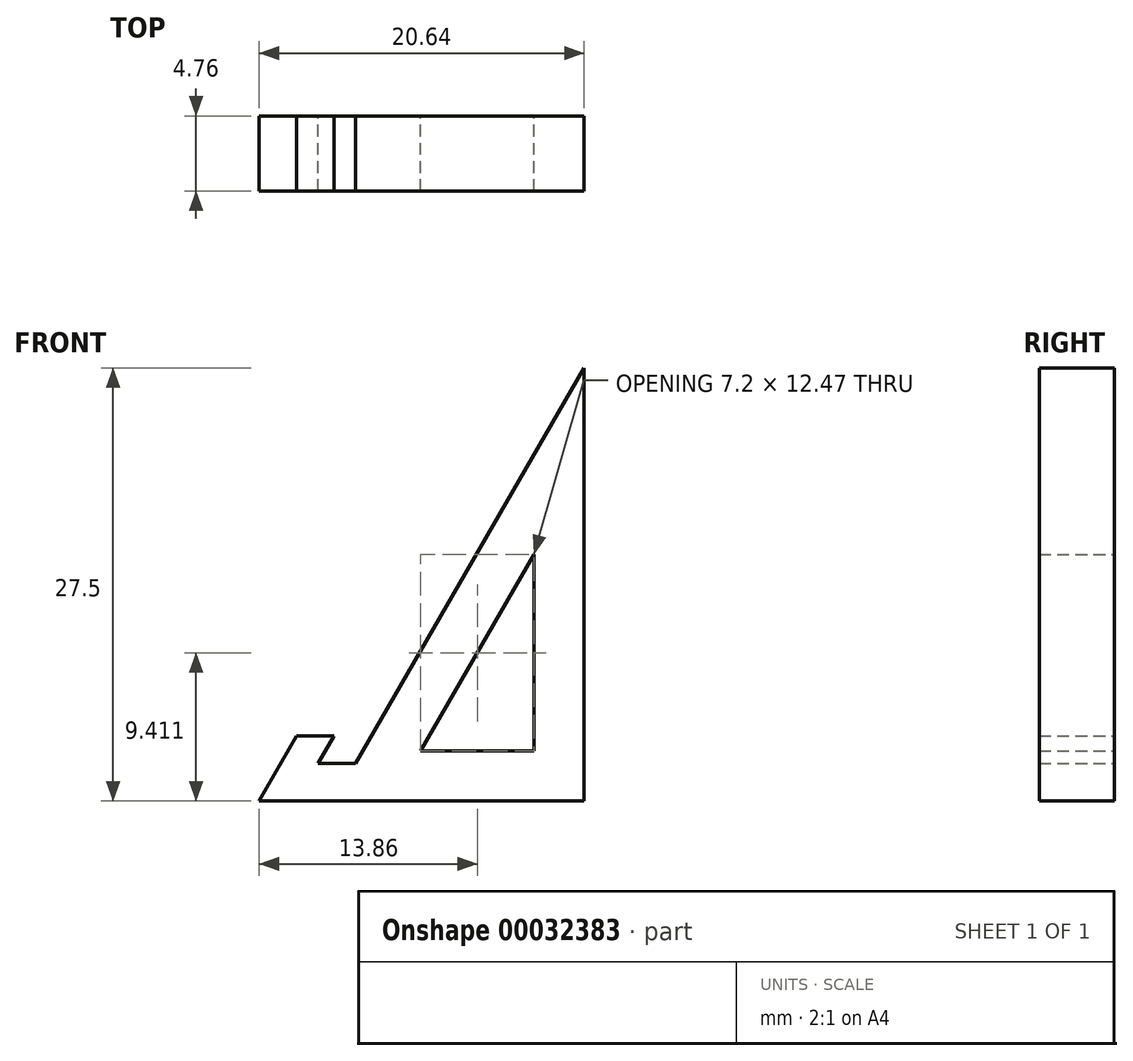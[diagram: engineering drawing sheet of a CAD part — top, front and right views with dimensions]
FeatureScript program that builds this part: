
annotation { "Feature Type Name" : "Feature", "Feature Type Description" : "" }
export const myFeature = defineFeature(function(context is Context, id is Id, definition is map)
    precondition{}
    {
        {
            var Q0;
            Q0=qCreatedBy(makeId("Front.planeOp"),FACE);
            var sketch = newSketch(context, id + "F0", { "sketchPlane" : qUnion([Q0])});
            skLineSegment(sketch, "E0", {"start": v(0, 0) * mm, "end": v(15.87, 0) * mm});
            skLineSegment(sketch, "E1", {"start": v(15.87, 0) * mm, "end": v(15.87, 27.5) * mm});
            skLineSegment(sketch, "E2", {"start": v(15.87, 27.5) * mm, "end": v(1.37, 2.38) * mm});
            skLineSegment(sketch, "E3.0", {"start": v(5.5, 3.18) * mm, "end": v(12.7, 3.18) * mm});
            skLineSegment(sketch, "E3.1", {"start": v(12.7, 15.65) * mm, "end": v(5.5, 3.17) * mm});
            skLineSegment(sketch, "E3.2", {"start": v(12.7, 3.18) * mm, "end": v(12.7, 15.65) * mm});
            skLineSegment(sketch, "E4", {"start": v(0, 0) * mm, "end": v(-4.76, 0) * mm});
            skLineSegment(sketch, "E5", {"start": v(-4.76, 0) * mm, "end": v(-2.38, 4.12) * mm});
            skLineSegment(sketch, "E6", {"start": v(-2.38, 4.12) * mm, "end": v(0, 4.12) * mm});
            skLineSegment(sketch, "E7", {"start": v(0, 4.12) * mm, "end": v(-1, 2.38) * mm});
            skLineSegment(sketch, "E8", {"start": v(-1, 2.38) * mm, "end": v(1.37, 2.38) * mm});
            skSolve(sketch);
        }
        {
            var Q0;
            Q0 = qSketchRegion(id + "F0", true);
            extrude(context, id + "F1", {"entities" : qUnion([Q0]), "depth" : 4.76 * mm});
        }
    });
